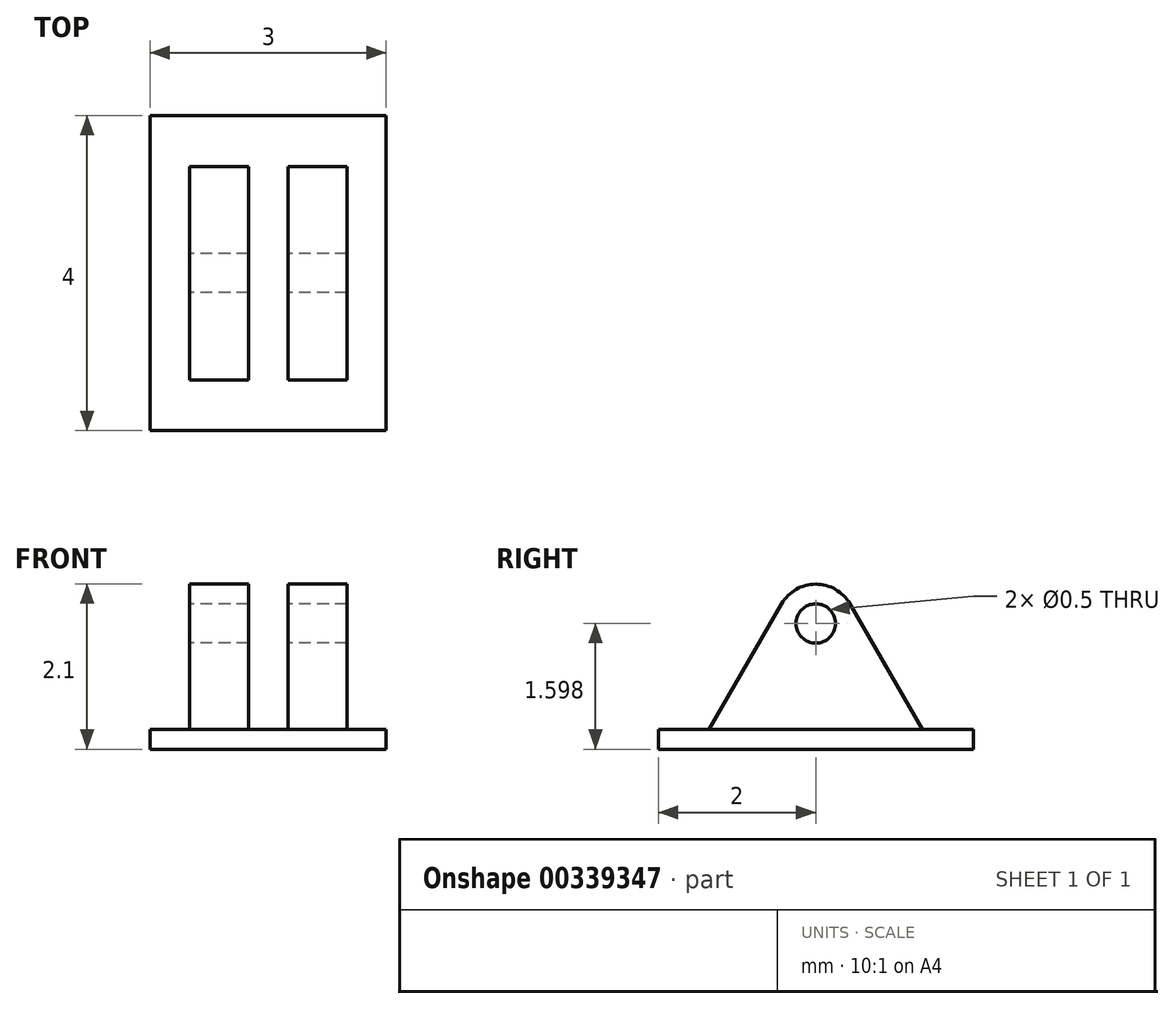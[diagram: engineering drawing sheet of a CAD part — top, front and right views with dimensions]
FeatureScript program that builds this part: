
annotation { "Feature Type Name" : "Feature", "Feature Type Description" : "" }
export const myFeature = defineFeature(function(context is Context, id is Id, definition is map)
    precondition{}
    {
        {
            var Q0;
            Q0=qCreatedBy(makeId("Right.planeOp"),FACE);
            var sketch = newSketch(context, id + "F0", { "sketchPlane" : qUnion([Q0])});
            skLineSegment(sketch, "E0", {"start": v(-1.5, 0) * mm, "end": v(-0.43, 1.85) * mm});
            skLineSegment(sketch, "E1.MirrorCS", {"start": v(1.5, 0) * mm, "end": v(0.43, 1.85) * mm});
            skArc(sketch, "E2", {"start": v(0.43, 1.85) * mm, "mid": v(0, 2.1) * mm, "end": v(-0.43, 1.85) * mm});
            skPoint(sketch, "E2.first.point", {"position": v(-0.43, 1.85) * mm});
            skPoint(sketch, "E2.second.point", {"position": v(0.43, 1.85) * mm});
            skPoint(sketch, "E2.third.point", {"position": v(0.43, 1.85) * mm});
            skCircle(sketch, "E3", {"center": v(0, 1.6) * mm, "radius": 0.25 * mm});
            skPoint(sketch, "E4.orphan", {"position": v(0, 2.6) * mm});
            skLineSegment(sketch, "E5", {"start": v(-1.5, 0) * mm, "end": v(1.5, 0) * mm});
            skSolve(sketch);
        }
        {
            var Q0;
            Q0=makeQuery(id+"F0.imprint","IMPRINT",FACE,{"disambiguationData":[TD([[makeQuery(id+"F0.imprint","IMPRINT",EDGE,{"derivedFrom":sQuery(id+"F0.wireOp",EDGE,"E0")}),-1.0]])]});
            extrude(context, id + "F1", {"entities" : qUnion([Q0]), "endBound" : BoundingType.SYMMETRIC, "depth" : 2 * mm});
        }
        {
            var Q0;
            Q0=qCreatedBy(makeId("Front.planeOp"),FACE);
            var sketch = newSketch(context, id + "F2", { "sketchPlane" : qUnion([Q0])});
            skLineSegment(sketch, "E6.bottom", {"start": v(0.25, 2.2) * mm, "end": v(-0.25, 2.2) * mm});
            skLineSegment(sketch, "E6.top", {"start": v(0.25, -0.41) * mm, "end": v(-0.25, -0.41) * mm});
            skLineSegment(sketch, "E6.left", {"start": v(0.25, 2.2) * mm, "end": v(0.25, -0.41) * mm});
            skLineSegment(sketch, "E6.right", {"start": v(-0.25, 2.2) * mm, "end": v(-0.25, -0.41) * mm});
            skPoint(sketch, "E6.middle", {"position": v(0, 0.89) * mm});
            skSolve(sketch);
        }
        {
            var Q0;
            Q0=makeQuery(id+"F2.imprint","IMPRINT",FACE,{"disambiguationData":[TD([[makeQuery(id+"F2.imprint","IMPRINT",EDGE,{"derivedFrom":sQuery(id+"F2.wireOp",EDGE,"E6.bottom")}),1.0]])]});
            extrude(context, id + "F3", {"entities" : qUnion([Q0]), "operationType" : NewBodyOperationType.REMOVE, "endBound" : BoundingType.SYMMETRIC, "depth" : 25 * mm});
        }
        {
            var Q0;
            Q0=qCreatedBy(makeId("Top.planeOp"),FACE);
            var sketch = newSketch(context, id + "F4", { "sketchPlane" : qUnion([Q0])});
            skLineSegment(sketch, "E7.bottom", {"start": v(-1.5, -2) * mm, "end": v(1.5, -2) * mm});
            skLineSegment(sketch, "E7.top", {"start": v(-1.5, 2) * mm, "end": v(1.5, 2) * mm});
            skLineSegment(sketch, "E7.left", {"start": v(-1.5, -2) * mm, "end": v(-1.5, 2) * mm});
            skLineSegment(sketch, "E7.right", {"start": v(1.5, -2) * mm, "end": v(1.5, 2) * mm});
            skPoint(sketch, "E7.middle", {"position": v(0, 0) * mm});
            skSolve(sketch);
        }
        {
            var Q0;
            Q0=makeQuery(id+"F4.imprint","IMPRINT",FACE,{"disambiguationData":[TD([[makeQuery(id+"F4.imprint","IMPRINT",EDGE,{"derivedFrom":sQuery(id+"F4.wireOp",EDGE,"E7.bottom")}),1.0]])]});
            extrude(context, id + "F5", {"entities" : qUnion([Q0]), "operationType" : NewBodyOperationType.ADD, "depth" : .25 * mm});
        }
    });
